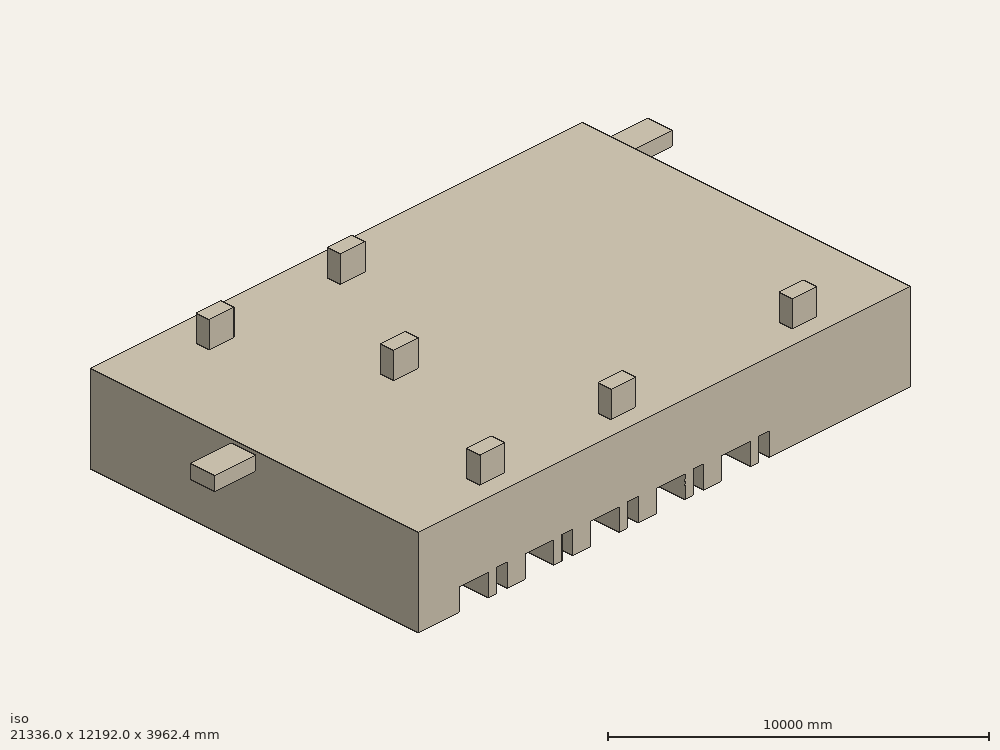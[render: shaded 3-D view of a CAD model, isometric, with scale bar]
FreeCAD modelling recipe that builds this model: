
FCSTD DOCUMENT  (FreeCAD 0.18R14555 (Git shallow))
Label: flow_domain
License: All rights reserved
LicenseURL: http://en.wikipedia.org/wiki/All_rights_reserved
objects: Part::Box×20, Part::MultiFuse×12, Part::Mirroring×1, Part::Cut×1
note: 34 computed .brp shape members not serialized (recipe doc carries the construction recipe); baked Part::Feature solids carry a one-line shape summary decoded from their .brp

FEATURE [Part::Box] Box001  label="Bed 1"
  AttacherType = Attacher::AttachEngine3D
  Height = 762
  Length = 1066.8
  Width = 1981.2
FEATURE [Part::Box] Box002  label="Table 1"
  AttacherType = Attacher::AttachEngine3D
  Height = 798.576
  Length = 396.24
  Placement = pos=(1371.6,0,0) rot=(0,0,1;0rad)
  Width = 396.24
FEATURE [Part::MultiFuse] Fusion  label="Set 1"
  Shapes = -> [Box002,Box001]
FEATURE [Part::Box] Box003  label="Bed 002"
  AttacherType = Attacher::AttachEngine3D
  Height = 762
  Length = 1066.8
  Width = 1981.2
FEATURE [Part::Box] Box004  label="Table 002"
  AttacherType = Attacher::AttachEngine3D
  Height = 798.576
  Length = 396.24
  Placement = pos=(1371.6,0,0) rot=(0,0,1;0rad)
  Width = 396.24
FEATURE [Part::MultiFuse] Fusion001  label="Set 2"
  Placement = pos=(2438.4,0,0) rot=(0,0,1;0rad)
  Shapes = -> [Box004,Box003]
FEATURE [Part::Box] Box005  label="Table 003"
  AttacherType = Attacher::AttachEngine3D
  Height = 798.576
  Length = 396.24
  Placement = pos=(1371.6,0,0) rot=(0,0,1;0rad)
  Width = 396.24
FEATURE [Part::Box] Box006  label="Bed 003"
  AttacherType = Attacher::AttachEngine3D
  Height = 762
  Length = 1066.8
  Width = 1981.2
FEATURE [Part::MultiFuse] Fusion002  label="Set 3"
  Placement = pos=(4876.8,0,0) rot=(0,0,1;0rad)
  Shapes = -> [Box005,Box006]
FEATURE [Part::Box] Box007  label="Bed 004"
  AttacherType = Attacher::AttachEngine3D
  Height = 762
  Length = 1066.8
  Width = 1981.2
FEATURE [Part::Box] Box008  label="Table 004"
  AttacherType = Attacher::AttachEngine3D
  Height = 798.576
  Length = 396.24
  Placement = pos=(1371.6,0,0) rot=(0,0,1;0rad)
  Width = 396.24
FEATURE [Part::MultiFuse] Fusion003  label="Set 4"
  Placement = pos=(7315.2,0,0) rot=(0,0,1;0rad)
  Shapes = -> [Box008,Box007]
FEATURE [Part::Box] Box009  label="Table 005"
  AttacherType = Attacher::AttachEngine3D
  Height = 798.576
  Length = 396.24
  Placement = pos=(1371.6,0,0) rot=(0,0,1;0rad)
  Width = 396.24
FEATURE [Part::Box] Box010  label="Bed 005"
  AttacherType = Attacher::AttachEngine3D
  Height = 762
  Length = 1066.8
  Width = 1981.2
FEATURE [Part::MultiFuse] Fusion004  label="Set 5"
  Placement = pos=(9753.6,0,0) rot=(0,0,1;0rad)
  Shapes = -> [Box009,Box010]
FEATURE [Part::MultiFuse] Fusion005  label="right beds"
  Shapes = -> [Fusion001,Fusion002,Fusion003,Fusion004,Fusion]
FEATURE [Part::Mirroring] Part__Mirroring  label="left beds"
  Base = (0,6096,0)
  Normal = (0,1,0)
  Source = -> Fusion005
FEATURE [Part::Box] Box011  label="Nurse Station"
  AttacherType = Attacher::AttachEngine3D
  Height = 1219.2
  Length = 3048
  Placement = pos=(15240,7620,0) rot=(0,0,1;0rad)
  Width = 4572
FEATURE [Part::Box] Box013  label="main outlet"
  AttacherType = Attacher::AttachEngine3D
  Height = 487.68
  Length = 2438.4
  Placement = pos=(-1524,6040.43,2438.4) rot=(0,0,1;0rad)
  Width = 914.4
FEATURE [Part::Box] Box016  label="branch002"
  AttacherType = Attacher::AttachEngine3D
  Height = 1219.2
  Length = 914.4
  Placement = pos=(7772.4,609.6,2743.2) rot=(0,0,1;0rad)
  Width = 487.68
FEATURE [Part::Box] Box017  label="branch003"
  AttacherType = Attacher::AttachEngine3D
  Height = 1219.2
  Length = 914.4
  Placement = pos=(7772.4,10668,2743.2) rot=(0,0,1;0rad)
  Width = 487.68
FEATURE [Part::Box] Box018  label="branch004"
  AttacherType = Attacher::AttachEngine3D
  Height = 1219.2
  Length = 914.4
  Placement = pos=(2895.6,609.6,2743.2) rot=(0,0,1;0rad)
  Width = 487.68
FEATURE [Part::Box] Box019  label="branch005"
  AttacherType = Attacher::AttachEngine3D
  Height = 1219.2
  Length = 914.4
  Placement = pos=(2895.6,10668,2743.2) rot=(0,0,1;0rad)
  Width = 487.68
FEATURE [Part::MultiFuse] Fusion006  label="all beds"
  Placement = pos=(1524,0,0) rot=(0,0,1;0rad)
  Shapes = -> [Part__Mirroring,Fusion005]
FEATURE [Part::Box] Box  label="Room"
  AttacherType = Attacher::AttachEngine3D
  Height = 3048
  Length = 18288
  Width = 12192
FEATURE [Part::MultiFuse] Fusion010  label="surfaces"
  Shapes = -> [Fusion006,Box011]
FEATURE [Part::Box] Box020  label="main inlet001"
  AttacherType = Attacher::AttachEngine3D
  Height = 487.68
  Length = 2438.4
  Placement = pos=(17373.6,10363.2,2438.4) rot=(0,0,1;0rad)
  Width = 914.4
FEATURE [Part::Box] Box021  label="branch006"
  AttacherType = Attacher::AttachEngine3D
  Height = 1219.2
  Length = 914.4
  Placement = pos=(5181.6,6096,2743.2) rot=(0,0,1;0rad)
  Width = 487.68
FEATURE [Part::Box] Box022  label="branch007"
  AttacherType = Attacher::AttachEngine3D
  Height = 1219.2
  Length = 914.4
  Placement = pos=(14506.5,609.6,2743.2) rot=(0,0,1;0rad)
  Width = 487.68
FEATURE [Part::MultiFuse] Fusion011
  Shapes = -> [Box016,Box017,Box018,Box019,Box021,Box022]
FEATURE [Part::MultiFuse] Fusion012
  Shapes = -> [Box013,Box020]
FEATURE [Part::MultiFuse] Fusion013
  Shapes = -> [Fusion012,Fusion011]
FEATURE [Part::MultiFuse] Fusion014
  Shapes = -> [Fusion013,Box]
FEATURE [Part::Cut] Cut
  Base = -> Fusion014
  Tool = -> Fusion010
